# Revit family: Plumbing Fixture_Red Emperor_Rain Water Outlet_Vert-Dome
name_source: partatom
category: Plumbing Fixtures
revit_build: Autodesk Revit 2015 (Build: 20151207_1515(x64)
units: mm (PartAtom-declared; Revit-internal decimal feet)

## types (2) — shared parameters
A = 112 mm  [stored 0.367454 ft]
E = 120 mm  [stored 0.393701 ft]
Manufacturer = Red Emperor
Manufacturer_URL__Product Specific = http://www.red-emperor.com.au
Material_ANZRS = z_Red Emperor_Grey
URL = http://www.red-emperor.com.au

## per-type parameters (varying)
| type | Description | Manufacturer_Overall Depth | Manufacturer_Overall Height | Manufacturer_Overall Width | Manufacturer_Spec Code | Model | Pipe Dia | Pipe Radius | Radius |
| 260Wx260Dx100H 285205 | Ductile Iron Multi-Purpose Heavy Duty Domed Vertical Rain Water Outlet (with Membrane Clamp Ring) 100 PVC/HDPE. | 260 mm  [stored 0.853018 ft] | 100 mm  [stored 0.328084 ft] | 260 mm  [stored 0.853018 ft] | 285205 | 285205 | 100 mm  [stored 0.328084 ft] | 50 mm  [stored 0.164042 ft] | 130 mm  [stored 0.426509 ft] |
| 270Wx270Dx98H 285219 | Ductile Iron Multi-Purpose Heavy Duty Domed Vertical Rain Water Outlet (with Membrane Clamp Ring) 150 PVC/HDPE. | 270 mm  [stored 0.885827 ft] | 98 mm  [stored 0.321522 ft] | 270 mm  [stored 0.885827 ft] | 285219 | 285219 | 150 mm | 75 mm | 135 mm  [stored 0.442913 ft] |

note: [stored X ft] marks values corroborated as IEEE doubles in the binary element streams (Revit-internal decimal feet)

## geometry (parser evidence)
native form markers: Sweep x4
no freeform markers — native parametric forms only
